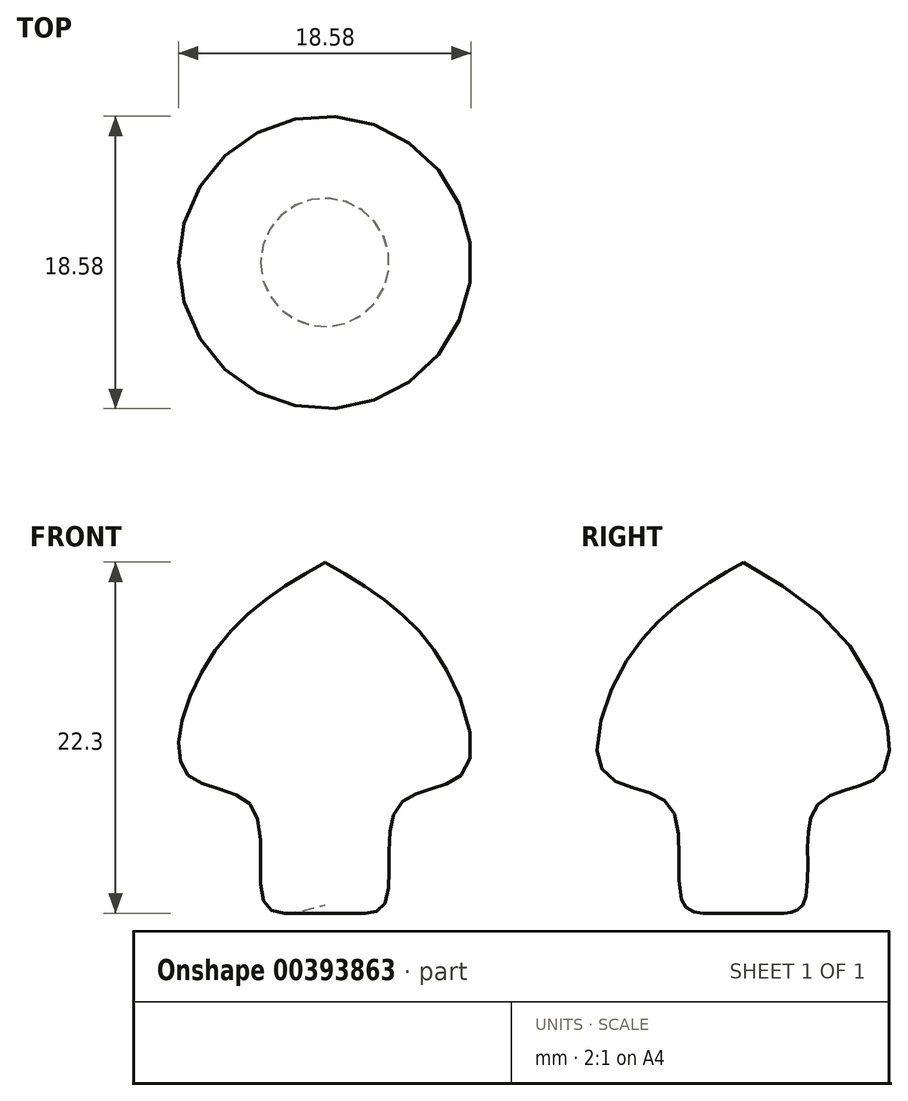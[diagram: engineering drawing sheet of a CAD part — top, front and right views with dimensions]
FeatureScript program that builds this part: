
annotation { "Feature Type Name" : "Feature", "Feature Type Description" : "" }
export const myFeature = defineFeature(function(context is Context, id is Id, definition is map)
    precondition{}
    {
        {
            var Q0;
            Q0=qCreatedBy(makeId("Front.planeOp"),FACE);
            var sketch = newSketch(context, id + "F0", { "sketchPlane" : qUnion([Q0])});
            skLineSegment(sketch, "E0", {"start": v(0, 0) * mm, "end": v(0, 21.76) * mm});
            skFitSpline(sketch, "E1", {"points": [v(0, 21.76) * mm, v(-7.11, 15.94) * mm, v(-8.79, 8.34) * mm, v(-4.6, 6.2) * mm, v(-3.77, 0) * mm, v(0, 0) * mm], "startDerivative": vector(-32.1, -18.69) * mm, "endDerivative": vector(30.61, 8.94) * mm});
            skSolve(sketch);
        }
        {
            var Q0;
            Q0 = qSketchRegion(id + "F0", true);
            var Q1;
            Q1=sQuery(id+"F0.wireOp",EDGE,"E0");
            revolve(context, id + "F1", {"entities" : qUnion([Q0]), "axis" : qUnion([Q1]), "revolveType" : RevolveType.FULL});
        }
    });
